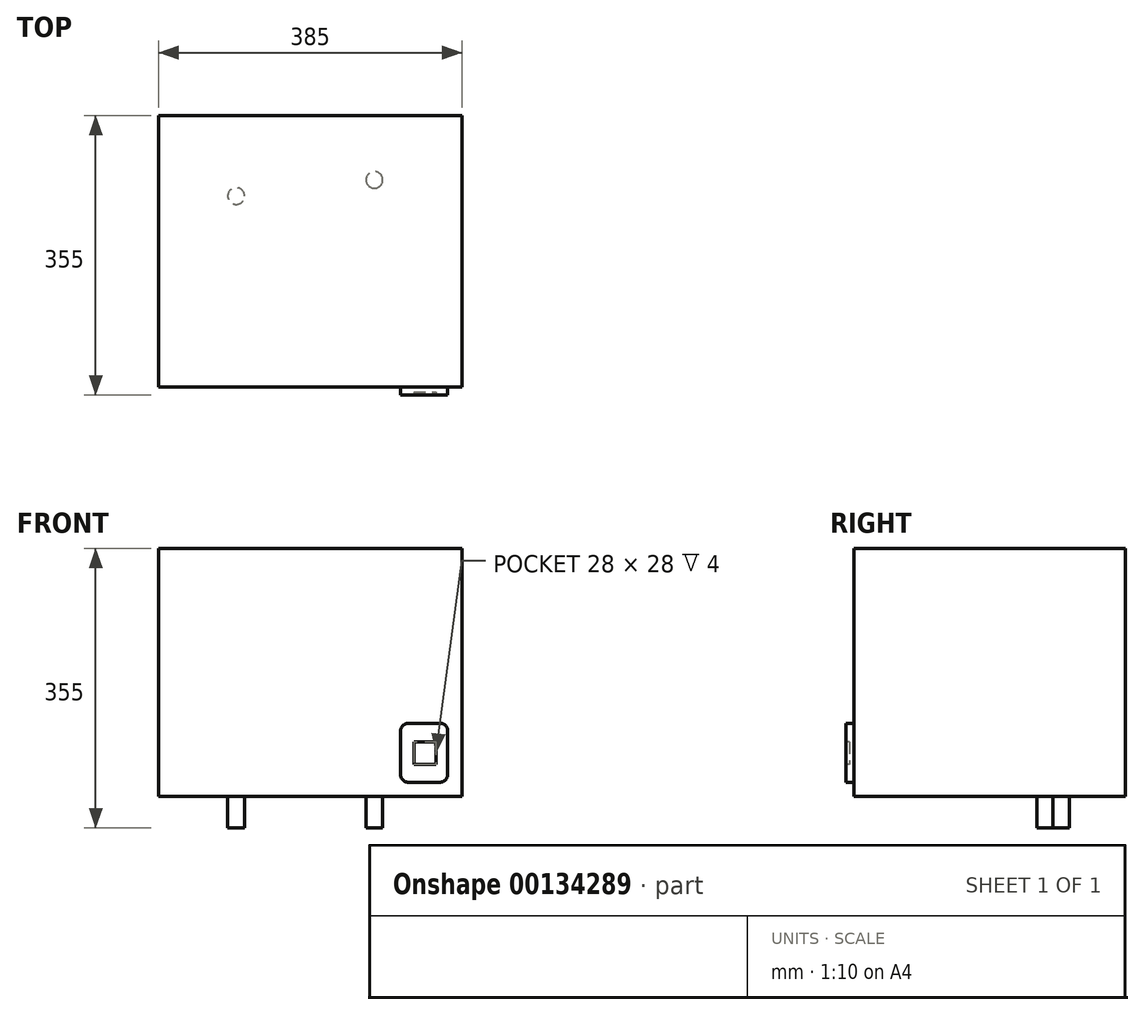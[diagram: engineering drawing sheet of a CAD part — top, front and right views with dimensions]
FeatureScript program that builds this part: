
annotation { "Feature Type Name" : "Feature", "Feature Type Description" : "" }
export const myFeature = defineFeature(function(context is Context, id is Id, definition is map)
    precondition{}
    {
        {
            var Q0;
            Q0=qCreatedBy(makeId("Front.planeOp"),FACE);
            var sketch = newSketch(context, id + "F0", { "sketchPlane" : qUnion([Q0])});
            skLineSegment(sketch, "E0.bottom", {"start": v(0, 0) * mm, "end": v(385, 0) * mm});
            skLineSegment(sketch, "E0.top", {"start": v(0, 315) * mm, "end": v(385, 315) * mm});
            skLineSegment(sketch, "E0.left", {"start": v(0, 0) * mm, "end": v(0, 315) * mm});
            skLineSegment(sketch, "E0.right", {"start": v(385, 0) * mm, "end": v(385, 315) * mm});
            skSolve(sketch);
        }
        {
            var Q0;
            Q0 = qSketchRegion(id + "F0", true);
            extrude(context, id + "F1", {"entities" : qUnion([Q0]), "depth" : 345 * mm});
        }
        {
            var Q0;
            Q0=makeQuery(id+"F1.opExtrude","CAP_FACE",FACE,{"disambiguationData":[OSD([sQuery(id+"F0.wireOp",EDGE,"E0.bottom"),sQuery(id+"F0.wireOp",EDGE,"E0.top"),sQuery(id+"F0.wireOp",EDGE,"E0.left"),sQuery(id+"F0.wireOp",EDGE,"E0.right")])],"isStart":false});
            var sketch = newSketch(context, id + "F2", { "sketchPlane" : qUnion([Q0])});
            skLineSegment(sketch, "E1.bottom", {"start": v(307, 93) * mm, "end": v(367, 93) * mm});
            skLineSegment(sketch, "E1.top", {"start": v(307, 18) * mm, "end": v(367, 18) * mm});
            skLineSegment(sketch, "E1.left", {"start": v(307, 93) * mm, "end": v(307, 18) * mm});
            skLineSegment(sketch, "E1.right", {"start": v(367, 93) * mm, "end": v(367, 18) * mm});
            skSolve(sketch);
        }
        {
            var Q0;
            Q0 = qSketchRegion(id + "F2", true);
            extrude(context, id + "F3", {"entities" : qUnion([Q0]), "operationType" : NewBodyOperationType.ADD, "depth" : 10 * mm});
        }
        {
            var Q0;
            Q0=makeQuery(id+"F3.opExtrude","SWEPT_EDGE",EDGE,{"disambiguationData":[OSD([sQuery(id+"F2.wireOp",EDGE,"E1.bottom"),sQuery(id+"F2.wireOp",EDGE,"E1.right")])]});
            var Q1;
            Q1=makeQuery(id+"F3.opExtrude","SWEPT_EDGE",EDGE,{"disambiguationData":[OSD([sQuery(id+"F2.wireOp",EDGE,"E1.top"),sQuery(id+"F2.wireOp",EDGE,"E1.right")])]});
            var Q2;
            Q2=makeQuery(id+"F3.opExtrude","SWEPT_EDGE",EDGE,{"disambiguationData":[OSD([sQuery(id+"F2.wireOp",EDGE,"E1.bottom"),sQuery(id+"F2.wireOp",EDGE,"E1.left")])]});
            var Q3;
            Q3=makeQuery(id+"F3.opExtrude","SWEPT_EDGE",EDGE,{"disambiguationData":[OSD([sQuery(id+"F2.wireOp",EDGE,"E1.top"),sQuery(id+"F2.wireOp",EDGE,"E1.left")])]});
            fillet(context, id + "F4", {"entities" : qUnion([Q0, Q1, Q2, Q3]), "radius" : 10 * mm, "tangentPropagation" : true, "allowEdgeOverflow" : false});
        }
        {
            var Q0;
            Q0=makeQuery(id+"F3.opExtrude","CAP_FACE",FACE,{"disambiguationData":[OSD([sQuery(id+"F2.wireOp",EDGE,"E1.bottom"),sQuery(id+"F2.wireOp",EDGE,"E1.top"),sQuery(id+"F2.wireOp",EDGE,"E1.left"),sQuery(id+"F2.wireOp",EDGE,"E1.right")])],"isStart":false});
            var sketch = newSketch(context, id + "F5", { "sketchPlane" : qUnion([Q0])});
            skLineSegment(sketch, "E2.bottom", {"start": v(324, 69) * mm, "end": v(352, 69) * mm});
            skLineSegment(sketch, "E2.top", {"start": v(324, 41) * mm, "end": v(352, 41) * mm});
            skLineSegment(sketch, "E2.left", {"start": v(324, 69) * mm, "end": v(324, 41) * mm});
            skLineSegment(sketch, "E2.right", {"start": v(352, 69) * mm, "end": v(352, 41) * mm});
            skSolve(sketch);
        }
        {
            var Q0;
            Q0 = qSketchRegion(id + "F5", true);
            extrude(context, id + "F6", {"entities" : qUnion([Q0]), "operationType" : NewBodyOperationType.REMOVE, "oppositeDirection" : true, "depth" : 4 * mm});
        }
        {
            var Q0;
            Q0=makeQuery(id+"F1.opExtrude","SWEPT_FACE",FACE,{"disambiguationData":[OSD([sQuery(id+"F0.wireOp",EDGE,"E0.bottom")])]});
            var sketch = newSketch(context, id + "F7", { "sketchPlane" : qUnion([Q0])});
            skCircle(sketch, "E3", {"center": v(98.25, 102.25) * mm, "radius": 10.65 * mm});
            skSolve(sketch);
        }
        {
            var Q0;
            Q0 = qSketchRegion(id + "F7", true);
            extrude(context, id + "F8", {"entities" : qUnion([Q0]), "operationType" : NewBodyOperationType.ADD, "depth" : 40 * mm});
        }
        {
            var Q0;
            Q0=makeQuery(id+"F1.opExtrude","SWEPT_FACE",FACE,{"disambiguationData":[OSD([sQuery(id+"F0.wireOp",EDGE,"E0.bottom")])]});
            var sketch = newSketch(context, id + "F9", { "sketchPlane" : qUnion([Q0])});
            skCircle(sketch, "E4", {"center": v(273.86, 81.7) * mm, "radius": 10.65 * mm});
            skSolve(sketch);
        }
        {
            var Q0;
            Q0 = qSketchRegion(id + "F9", true);
            extrude(context, id + "F10", {"entities" : qUnion([Q0]), "operationType" : NewBodyOperationType.ADD, "depth" : 40 * mm});
        }
    });
